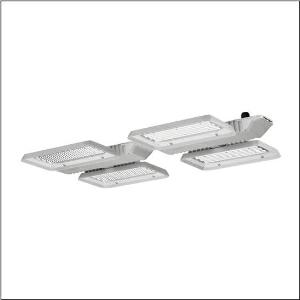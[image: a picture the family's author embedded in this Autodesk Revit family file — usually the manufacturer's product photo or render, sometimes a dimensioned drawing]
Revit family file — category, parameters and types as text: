
# Revit family: highbay_11_51hla2d24mca
name_source: partatom
category: Lighting Fixtures
units: mm (PartAtom-declared; Revit-internal decimal feet)

## family parameters
Cut with Voids When Loaded = No
Host = Face
Light Source = No
Part Type = Normal
Room Calculation Point = No
Round Connector Dimension = Use Diameter
Shared = No

## types (1)
- --- (1 x LED, 28800 lm, 162.4 W, 4000K)
    Apparent Load = 162 VA
    CIE Flux Codes = 89 96 99 100 100
    Color Rendering = 80
    Color Temperature = 4000K
    Default Elevation = 1800 mm
    Description = Highbay 11, LED high bay luminaire, primary light control with lens, of PMMA, light emission: direct distribution, primary light characteristic: symmetric, installation type: surface-mounted, suspended mounting, for 2x 2x LED, rated luminous flux: 28.800lm, luminous efficacy: 177lm/W, light colour: 840, colour temperature: 4000K, control gear: ECG DALI, with terminal, 5-pole, max. 2.5mm², mains connection: 230..240V, AC, 50/60Hz, rated input power: 162W, LED unit, of diecast aluminium, unplated, bead blasted, silver, length: 940mm, width: 500mm, height: 65mm, housing, of diecast aluminium, uncoated, bead blasted, silver, protection rating (complete): IP65, insulation class (complete): insulation class I (protective earthing), certification: CE, ENEC, VDE, UKCA, protection symbol: D, impact resistance: IK08 with glass or PC cover, permissible operating ambient temperature: -35..+55°C, reducing of maximum allowable ambient temperature of 5°C with ceiling mounting, corresponds to IFS (International Featured Standards) requirements for safety and quality in the food industry, packaging unit: 1 piece
    Height = 95 mm
    Lamp = 1 x LED
    Lamp Light Flux = 28800 lm
    Lamp Power = 162.4 W
    Lamp count = 1
    Length = 939 mm
    Luminous efficacy = 177 lm/W
    Manufacturer = Siteco
    ModVariant = No
    Model = 51HLA2D24MCA
    Mounting Place = Ceiling
    Mounting Type = Pendant
    Number of Poles = 1
    OnlyDefault = Yes
    Power Factor = 1
    Product Name = Highbay 11
    Product group = LED high bay luminaire
    ProductGroupID = 903
    Protection Class = Protection class I
    Protection Degree = IP 65
    RLX_Detail_Level = 1
    RLX_Emergency_Light_Flux = 0 lm
    RLX_Emergency_Type = 0
    RLX_Emergency_Type_DB = No
    RlxData = <blob elided: 96773 chars, md5=92e83d7a>
    Socket = socket
    Standby Power = 0 W
    System Light Flux = 28800 lm
    System Power = 162 W
    Type Comments = factory setting: luminous flux: 100 % | dim-lin: 254 | 460 mA
    Type Image = l_1003428.jpg
    URL = http://relux.com
    VarID = @adj_160065
    Voltage = 0 V
    Weight = 0.00 kg
    Width = 501 mm

## geometry (parser evidence)
native form markers: Blend x4, Sweep x13
no freeform markers — native parametric forms only
